# Revit family: Cabinet_Overhead-Wall_Cabinet_Moduline
name_source: partatom
category: Furniture
units: mm (PartAtom-declared; Revit-internal decimal feet)

## family parameters
Always vertical = Yes
Cut with Voids When Loaded = No
Enable Cutting in Views = No
OmniClass Number = 23.40.20.00
OmniClass Title = General Furniture and Specialties
Render Appearance Source = Family Geometry
Room Calculation Point = No
Shared = No
Work Plane-Based = No

## types (30) — shared parameters
Keynote = 12 35 00
Manufacturer = Moduline Aluminum Cabinets
Model = Pro II Overhead Wall Cabinets
Product Page URL = https://www.arcat.com
URL = https://modulinecabinets.com
zero-valued in all types: Default Elevation

## per-type parameters (varying)
| type | Depth | Description | Door Clearance | Height | Width |
| 18"H x 11"D x 30"W | 11 " | Modular Overhead Wall Cabinet, Double Door, 18" Height x 11" Depth x 30" Width | 15 " | 18 " | 30 " |
| 18"H x 11"D x 32"W | 11 " | Modular Overhead Wall Cabinet, Double Door, 18" Height x 11" Depth x 32" Width | 16 " | 18 " | 32 " |
| 18"H x 11"D x 36"W | 11 " | Modular Overhead Wall Cabinet, Double Door, 18" Height x 11" Depth x 36" Width | 18 " | 18 " | 36 " |
| 18"H x 15"D x 30"W | 15 " | Modular Overhead Wall Cabinet, Double Door, 18" Height x 15" Depth x 30" Width | 15 " | 18 " | 30 " |
| 18"H x 15"D x 32"W | 15 " | Modular Overhead Wall Cabinet, Double Door, 18" Height x 15" Depth x 32" Width | 16 " | 18 " | 32 " |
| 18"H x 15"D x 36"W | 15 " | Modular Overhead Wall Cabinet, Double Door, 18" Height x 15" Depth x 36" Width | 18 " | 18 " | 36 " |
| 18"H x 24"D x 30"W | 24 " | Modular Overhead Wall Cabinet, Double Door, 18" Height x 24" Depth x 30" Width | 15 " | 18 " | 30 " |
| 18"H x 24"D x 32"W | 24 " | Modular Overhead Wall Cabinet, Double Door, 18" Height x 24" Depth x 32" Width | 16 " | 18 " | 32 " |
| 18"H x 24"D x 36"W | 24 " | Modular Overhead Wall Cabinet, Double Door, 18" Height x 24" Depth x 36" Width | 18 " | 18 " | 36 " |
| 24"H x 11"D x 30"W | 11 " | Modular Overhead Wall Cabinet, Double Door, 24" Height x 11" Depth x 30" Width | 15 " | 24 " | 30 " |
| 24"H x 11"D x 32"W | 11 " | Modular Overhead Wall Cabinet, Double Door, 24" Height x 11" Depth x 32" Width | 16 " | 24 " | 32 " |
| 24"H x 11"D x 36"W | 11 " | Modular Overhead Wall Cabinet, Double Door, 24" Height x 11" Depth x 36" Width | 18 " | 24 " | 36 " |
| 24"H x 15"D x 30"W | 15 " | Modular Overhead Wall Cabinet, Double Door, 24" Height x 15" Depth x 30" Width | 15 " | 24 " | 30 " |
| 24"H x 15"D x 32"W | 15 " | Modular Overhead Wall Cabinet, Double Door, 24" Height x 15" Depth x 32" Width | 16 " | 24 " | 32 " |
| 24"H x 15"D x 36"W | 15 " | Modular Overhead Wall Cabinet, Double Door, 24" Height x 15" Depth x 36" Width | 18 " | 24 " | 36 " |
| 24"H x 24"D x 30"W | 24 " | Modular Overhead Wall Cabinet, Double Door, 24" Height x 24" Depth x 30" Width | 15 " | 24 " | 30 " |
| 24"H x 24"D x 32"W | 24 " | Modular Overhead Wall Cabinet, Double Door, 24" Height x 24" Depth x 32" Width | 16 " | 24 " | 32 " |
| 24"H x 24"D x 36"W | 24 " | Modular Overhead Wall Cabinet, Double Door, 24" Height x 24" Depth x 36" Width | 18 " | 24 " | 36 " |
| 30"H x 11"D x 30"W | 11 " | Modular Overhead Wall Cabinet, Double Door, 30" Height x 11" Depth x 30" Width | 15 " | 30 " | 30 " |
| 30"H x 11"D x 32"W | 11 " | Modular Overhead Wall Cabinet, Double Door, 30" Height x 11" Depth x 32" Width | 16 " | 30 " | 32 " |
| 30"H x 11"D x 36"W | 11 " | Modular Overhead Wall Cabinet, Double Door, 30" Height x 11" Depth x 36" Width | 18 " | 30 " | 36 " |
| 30"H x 15"D x 30"W | 15 " | Modular Overhead Wall Cabinet, Double Door, 30" Height x 15" Depth x 30" Width | 15 " | 30 " | 30 " |
| 30"H x 15"D x 32"W | 15 " | Modular Overhead Wall Cabinet, Double Door, 30" Height x 15" Depth x 32" Width | 16 " | 30 " | 32 " |
| 30"H x 15"D x 36"W | 15 " | Modular Overhead Wall Cabinet, Double Door, 30" Height x 15" Depth x 36" Width | 18 " | 30 " | 36 " |
| 36"H x 11"D x 30"W | 11 " | Modular Overhead Wall Cabinet, Double Door, 36" Height x 11" Depth x 30" Width | 15 " | 36 " | 30 " |
| 36"H x 11"D x 32"W | 11 " | Modular Overhead Wall Cabinet, Double Door, 36" Height x 11" Depth x 32" Width | 16 " | 36 " | 32 " |
| 36"H x 11"D x 36"W | 11 " | Modular Overhead Wall Cabinet, Double Door, 36" Height x 11" Depth x 36" Width | 18 " | 36 " | 36 " |
| 36"H x 15"D x 30"W | 15 " | Modular Overhead Wall Cabinet, Double Door, 36" Height x 15" Depth x 30" Width | 15 " | 36 " | 30 " |
| 36"H x 15"D x 32"W | 15 " | Modular Overhead Wall Cabinet, Double Door, 36" Height x 15" Depth x 32" Width | 16 " | 36 " | 32 " |
| 36"H x 15"D x 36"W | 15 " | Modular Overhead Wall Cabinet, Double Door, 36" Height x 15" Depth x 36" Width | 18 " | 36 " | 36 " |

## geometry (parser evidence)
native form markers: Sweep x4
no freeform markers — native parametric forms only
